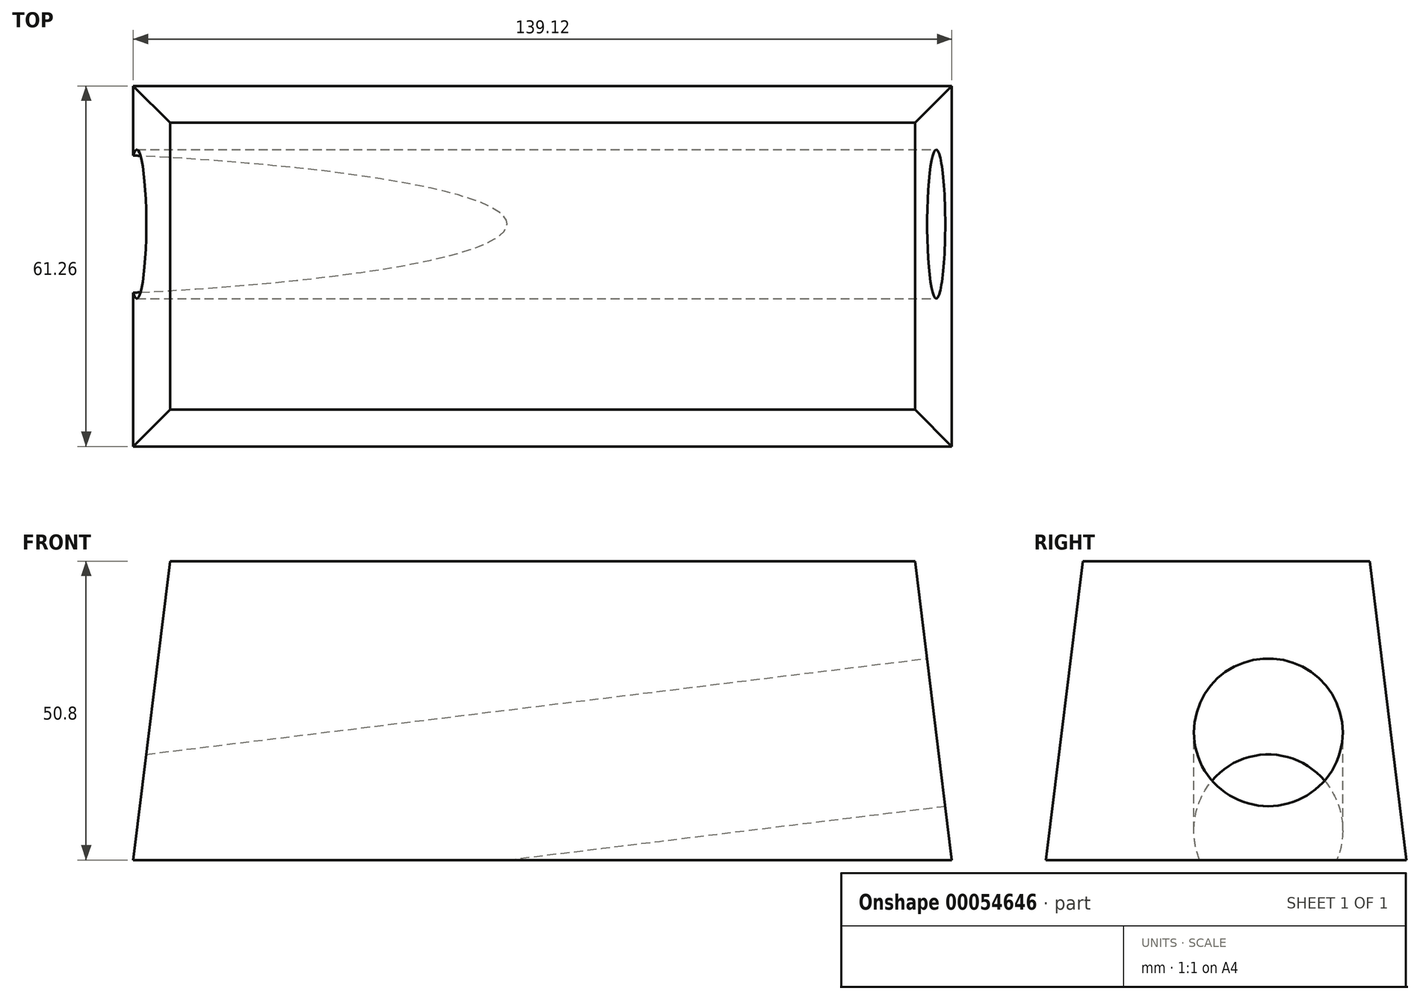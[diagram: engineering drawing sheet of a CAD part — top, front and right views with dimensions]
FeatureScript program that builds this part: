
annotation { "Feature Type Name" : "Feature", "Feature Type Description" : "" }
export const myFeature = defineFeature(function(context is Context, id is Id, definition is map)
    precondition{}
    {
        {
            var Q0;
            Q0=qCreatedBy(makeId("Top.planeOp"),FACE);
            var sketch = newSketch(context, id + "F0", { "sketchPlane" : qUnion([Q0])});
            skLineSegment(sketch, "E0.rect.bottom", {"start": v(40.3, -16.4) * mm, "end": v(179.41, -16.4) * mm});
            skLineSegment(sketch, "E0.rect.top", {"start": v(40.3, -77.67) * mm, "end": v(179.41, -77.67) * mm});
            skLineSegment(sketch, "E0.rect.left", {"start": v(40.3, -16.4) * mm, "end": v(40.3, -77.67) * mm});
            skLineSegment(sketch, "E0.rect.right", {"start": v(179.41, -16.4) * mm, "end": v(179.41, -77.67) * mm});
            skPoint(sketch, "E0.rect.middle", {"position": v(109.85, -47.04) * mm});
            skSolve(sketch);
        }
        {
            var Q0;
            Q0=makeQuery(id+"F0.imprint","IMPRINT",FACE,{"disambiguationData":[TD([[makeQuery(id+"F0.imprint","IMPRINT",EDGE,{"derivedFrom":sQuery(id+"F0.wireOp",EDGE,"E0.rect.bottom")}),-1.0]])]});
            extrude(context, id + "F1", {"entities" : qUnion([Q0]), "depth" : 50.8 * mm, "hasDraft" : true, "draftAngle" : 7 * degree, "draftPullDirection" : true});
        }
        {
            var Q0;
            Q0=makeQuery(id+"F1.opExtrude","SWEPT_FACE",FACE,{"disambiguationData":[OSD([sQuery(id+"F0.wireOp",EDGE,"E0.rect.right")])]});
            var sketch = newSketch(context, id + "F2", { "sketchPlane" : qUnion([Q0])});
            skCircle(sketch, "E1", {"center": v(-39.88, 0) * mm, "radius": 12.65 * mm});
            skSolve(sketch);
        }
        {
            var Q0;
            Q0=makeQuery(id+"F2.imprint","IMPRINT",FACE,{"disambiguationData":[TD([[makeQuery(id+"F2.imprint","IMPRINT",EDGE,{"derivedFrom":sQuery(id+"F2.wireOp",EDGE,"E1")}),1.0]])]});
            var Q1;
            Q1=makeQuery(id+"F1.opExtrude","SWEPT_FACE",FACE,{"disambiguationData":[OSD([sQuery(id+"F0.wireOp",EDGE,"E0.rect.left")])]});
            extrude(context, id + "F3", {"entities" : qUnion([Q0]), "operationType" : NewBodyOperationType.REMOVE, "endBound" : BoundingType.UP_TO_SURFACE, "oppositeDirection" : true, "endBoundEntityFace" : qUnion([Q1]), "depth" : 25.4 * mm});
        }
    });
